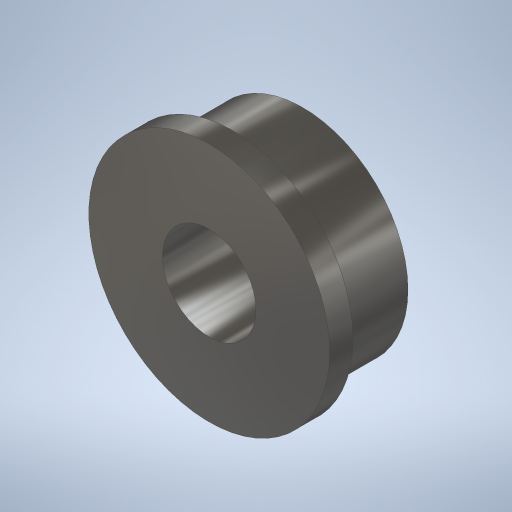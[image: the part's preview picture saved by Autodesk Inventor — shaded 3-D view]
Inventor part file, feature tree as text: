
AUTODESK INVENTOR PART (.ipt)
format: ipt  version: 2023 (Build 270158030, 158C)  size: 254,464 bytes
history: native  units: mm
features: extrude x2, sketch x2, other x1
ambient origin geometry x8: Origin, YZ Plane, XZ Plane, XY Plane, X Axis, Y Axis, Z Axis, Center Point
bodies: Body1 (feature_tree)
feature tree (5):
  other  "ソリッド1"
  extrude  "押し出し1"  Depth=4.0mm
  extrude  "押し出し2"  Depth=9.0mm
  sketch  "スケッチ1"
  sketch  "スケッチ2"
